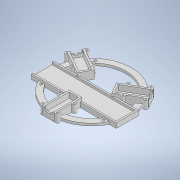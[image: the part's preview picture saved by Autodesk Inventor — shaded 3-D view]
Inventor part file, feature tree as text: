
AUTODESK INVENTOR PART (.ipt)
format: ipt  version: 2020.4 (Build 244396000, 396)  size: 487,936 bytes
history: native  units: mm
features: sketch x7, extrude x6, pattern_circular x1, hole x1, projected_geometry x1
ambient origin geometry x8: Origin, YZ Plane, XZ Plane, XY Plane, X Axis, Y Axis, Z Axis, Center Point
bodies: Solid1 (feature_tree)
feature tree (16):
  extrude  "Extrusion1"  Depth=86.0mm
  extrude  "Extrusion5"  Depth=7.0mm TaperAngle=0.0deg
  extrude  "Extrusion14"  Depth=9.0mm
  extrude  "Extrusion15"  Depth=2.0mm
  pattern_circular  "Circular Pattern3"  [2 undecoded]
  hole  "Hole1"  [1 undecoded]
  extrude  "Extrusion16"  Depth=0.5mm
  extrude  "Extrusion17"  Depth=0.5mm
  sketch  "Sketch1"  dims[d0=100.0mm d1=86.0mm]
  sketch  "Sketch6"  dims[d20=3.0mm d21=0.0mm d48=7.0mm d49=0.0mm]
  sketch  "Sketch7"  dims[d51=5.0mm d53=9.0mm]
  sketch  "Sketch11"  dims[d54=2.0mm d55=2.0mm]
  projected_geometry  "Projected Loop2"
  sketch  "Sketch16"  dims[d61=93.0mm]
  sketch  "Sketch17"  dims[d62=3.0mm]
  sketch  "Sketch18"  dims[d63=3.0mm d64=3.0mm d65=3.0mm d66=35.0mm d67=35.0mm d68=25.0mm d69=25.0mm d95=30.0mm d96=360.0deg d119=3.2mm d120=6.0mm d121=18.0mm d122=4.8mm d123=90.0deg d124=5.0mm d125=20.594885mm d147=12.0mm d148=30.0mm d149=2.0mm d150=30.0mm d152=360.0deg d154=24.0mm d156=2.0mm d157=10.0mm d158=0.0mm d159=5.0mm d162=25.8mm d163=2.0mm d164=1.5mm d165=16.0mm d166=20.0mm d168=18.0mm d169=20.0mm d171=21.0mm d174=10.0mm d175=0.0mm d176=103.0mm d177=24.0mm d178=2.0mm d179=3.0mm d180=10.0mm d181=0.0mm d182=2.0mm d183=3.0mm d184=0.0mm d126=0.5mm d127=0.872665mm d128=0.5mm d129=0.872665mm]
note: 3 required parameter values undecoded (feature->parameter linkage not recoverable at this tier; creation-order binding heuristic only, values carry confidence <= 0.55)
